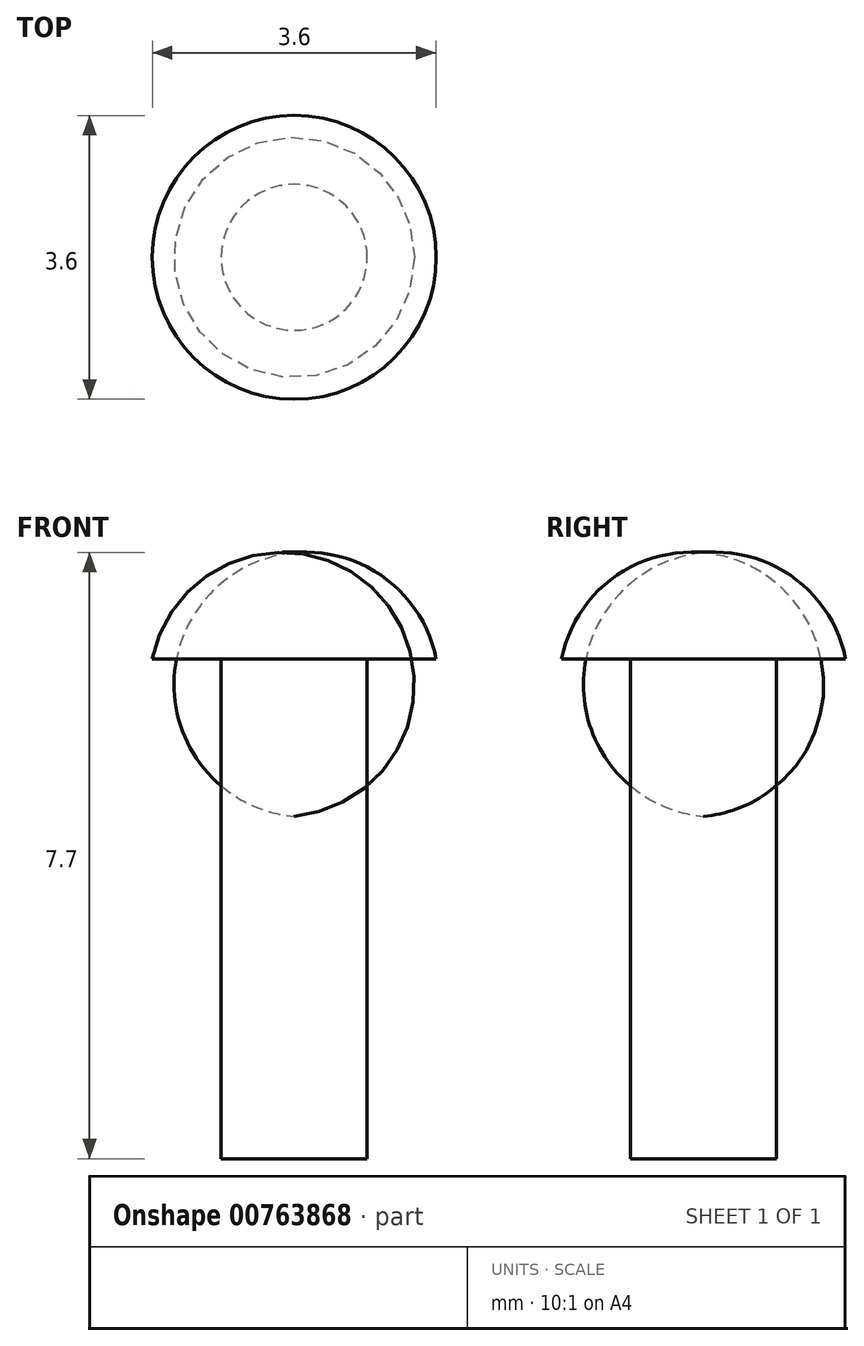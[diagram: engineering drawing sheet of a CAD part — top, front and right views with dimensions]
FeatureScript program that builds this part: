
annotation { "Feature Type Name" : "Feature", "Feature Type Description" : "" }
export const myFeature = defineFeature(function(context is Context, id is Id, definition is map)
    precondition{}
    {
        {
            var Q0;
            Q0=qCreatedBy(makeId("Top.planeOp"),FACE);
            var sketch = newSketch(context, id + "F0", { "sketchPlane" : qUnion([Q0])});
            skCircle(sketch, "E0", {"center": v(0, 0) * mm, "radius": 0.93 * mm});
            skSolve(sketch);
        }
        {
            var Q0;
            Q0 = qSketchRegion(id + "F0", true);
            extrude(context, id + "F1", {"entities" : qUnion([Q0]), "depth" : 6.35 * mm, "offsetDistance" : 25.4 * mm});
        }
        {
            var Q0;
            Q0=qCreatedBy(makeId("Front.planeOp"),FACE);
            var sketch = newSketch(context, id + "F2", { "sketchPlane" : qUnion([Q0])});
            skLineSegment(sketch, "E1", {"start": v(0, 6.35) * mm, "end": v(0, 7.7) * mm});
            skArc(sketch, "E2", {"start": v(1.8, 6.35) * mm, "mid": v(1.16, 7.37) * mm, "end": v(0, 7.7) * mm});
            skLineSegment(sketch, "E3.0", {"start": v(-0.93, 6.35) * mm, "end": v(0.93, 6.35) * mm});
            skLineSegment(sketch, "E4", {"start": v(0.93, 6.35) * mm, "end": v(1.8, 6.35) * mm});
            skSolve(sketch);
        }
        {
            var Q0;
            Q0 = qSketchRegion(id + "F2", true);
            var Q1;
            Q1=sQuery(id+"F2.wireOp",EDGE,"E1");
            revolve(context, id + "F3", {"operationType" : NewBodyOperationType.ADD, "surfaceOperationType" : NewSurfaceOperationType.NEW, "entities" : qUnion([Q0]), "axis" : qUnion([Q1]), "revolveType" : RevolveType.FULL});
        }
    });
